# Revit family: andreu_world_raglan_sf2119
name_source: partatom
category: Mobiliario
revit_build: Autodesk Revit 2018 (Build: 20170223_1515(x64)
units: mm (PartAtom-declared; Revit-internal decimal feet)

## family parameters
Compartido = No
Corte con vacíos al cargar = No
Número OmniClass = 23.40.20.00
Punto de cálculo de habitación = No
Se basa en plano de trabajo = No
Siempre vertical = Sí
Título OmniClass = General Furniture and Specialties

## types (1)
- andreu_world_raglan_sf2119
    Depth = 750 mm  [stored 2.46063 ft]
    Fabricante = Andreu World
    Height = 720 mm  [stored 2.3622 ft]
    Legs Height = 240 mm  [stored 0.787402 ft]
    Metal = Andreu World Polished Aluminum
    Modelo = Raglan
    Pipping = AW_Pipping
    Reference = SF-2119
    Seat Height = 430 mm
    URL = http://www.andreuworld.com
    Upholstery = AW_Fabric_Canvas 2_216
    Width = 1950 mm  [stored 6.39764 ft]

note: [stored X ft] marks values corroborated as IEEE doubles in the binary element streams (Revit-internal decimal feet)

## geometry (parser evidence)
native form markers: Blend x14, Sweep x2
no freeform markers — native parametric forms only
